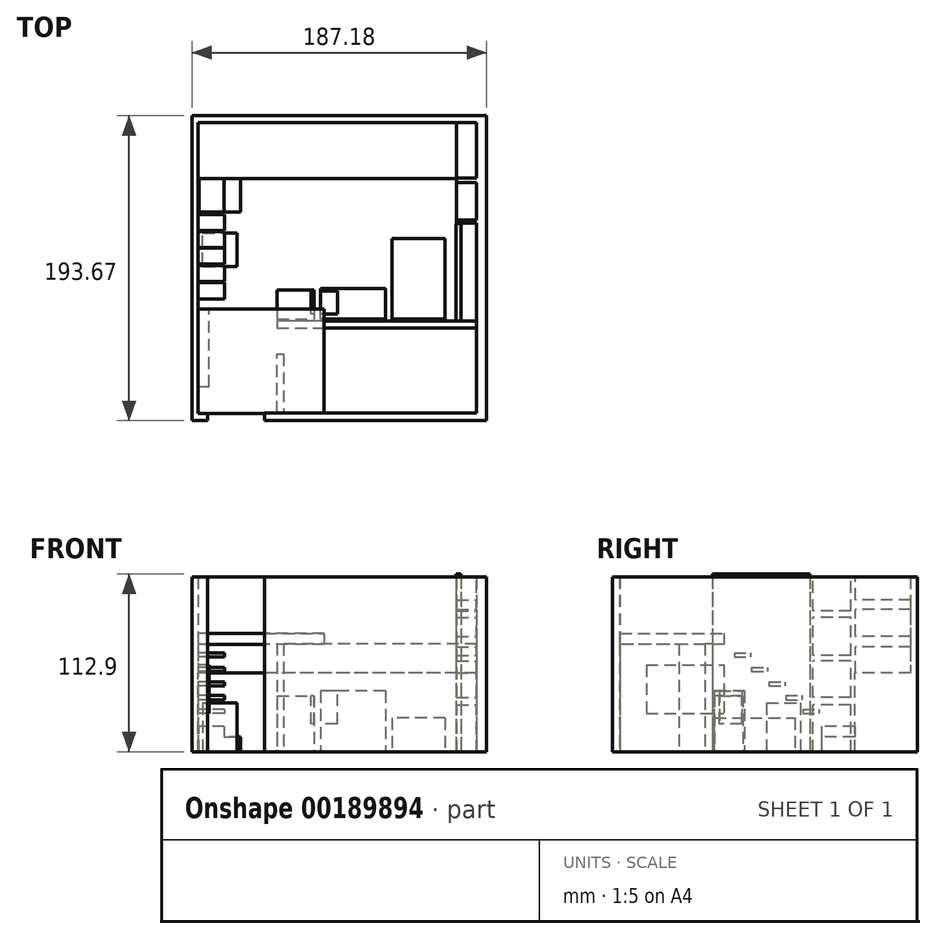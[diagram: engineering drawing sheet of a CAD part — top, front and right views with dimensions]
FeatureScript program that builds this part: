
annotation { "Feature Type Name" : "Feature", "Feature Type Description" : "" }
export const myFeature = defineFeature(function(context is Context, id is Id, definition is map)
    precondition{}
    {
        {
            var Q0;
            Q0=qCreatedBy(makeId("Top.planeOp"),FACE);
            var sketch = newSketch(context, id + "F0", { "sketchPlane" : qUnion([Q0])});
            skLineSegment(sketch, "E0", {"start": v(-29.04, -70.8) * mm, "end": v(-39.02, -70.8) * mm});
            skLineSegment(sketch, "E1", {"start": v(-39.02, -70.8) * mm, "end": v(-39.02, 122.87) * mm});
            skLineSegment(sketch, "E2", {"start": v(-39.02, 122.87) * mm, "end": v(148.16, 122.87) * mm});
            skLineSegment(sketch, "E3", {"start": v(148.16, 122.87) * mm, "end": v(148.16, -70.8) * mm});
            skLineSegment(sketch, "E4", {"start": v(148.16, -70.8) * mm, "end": v(7.05, -70.8) * mm});
            skLineSegment(sketch, "E5", {"start": v(7.05, -70.8) * mm, "end": v(7.05, -65.97) * mm});
            skLineSegment(sketch, "E6", {"start": v(7.05, -65.97) * mm, "end": v(141.88, -65.97) * mm});
            skLineSegment(sketch, "E7", {"start": v(141.88, -65.97) * mm, "end": v(141.88, 118.48) * mm});
            skLineSegment(sketch, "E8", {"start": v(141.88, 118.48) * mm, "end": v(-34.99, 118.48) * mm});
            skLineSegment(sketch, "E9", {"start": v(-34.99, 118.48) * mm, "end": v(-34.99, -66.3) * mm});
            skLineSegment(sketch, "E10", {"start": v(-34.99, -66.3) * mm, "end": v(-29.04, -66.3) * mm});
            skLineSegment(sketch, "E11", {"start": v(-29.04, -66.3) * mm, "end": v(-29.04, -70.8) * mm});
            skLineSegment(sketch, "E12", {"start": v(14.95, -65.97) * mm, "end": v(14.95, -28.61) * mm});
            skLineSegment(sketch, "E13", {"start": v(14.95, -28.61) * mm, "end": v(19.03, -28.61) * mm});
            skLineSegment(sketch, "E14", {"start": v(19.03, -28.61) * mm, "end": v(19.03, -65.97) * mm});
            skLineSegment(sketch, "E15", {"start": v(141.88, -7.47) * mm, "end": v(14.95, -7.47) * mm});
            skLineSegment(sketch, "E16", {"start": v(14.95, -7.47) * mm, "end": v(14.95, -12.15) * mm});
            skLineSegment(sketch, "E17", {"start": v(14.95, -12.15) * mm, "end": v(141.88, -12.15) * mm});
            skLineSegment(sketch, "E18", {"start": v(128.66, 54.4) * mm, "end": v(128.66, -7.47) * mm});
            skLineSegment(sketch, "E19", {"start": v(128.66, 54.4) * mm, "end": v(131.98, 54.4) * mm});
            skLineSegment(sketch, "E20", {"start": v(131.98, 54.4) * mm, "end": v(131.98, -7.47) * mm});
            skLineSegment(sketch, "E21.bottom", {"start": v(-34.45, 83.32) * mm, "end": v(-8.02, 83.32) * mm});
            skLineSegment(sketch, "E21.top", {"start": v(-34.45, 61.8) * mm, "end": v(-8.02, 61.8) * mm});
            skLineSegment(sketch, "E21.left", {"start": v(-34.45, 83.32) * mm, "end": v(-34.45, 61.8) * mm});
            skLineSegment(sketch, "E21.right", {"start": v(-8.02, 83.32) * mm, "end": v(-8.02, 61.8) * mm});
            skLineSegment(sketch, "E22.bottom", {"start": v(-8.02, 61.8) * mm, "end": v(-23.76, 61.8) * mm});
            skSolve(sketch);
        }
        {
            var Q0;
            Q0=makeQuery(id+"F0.imprint","IMPRINT",FACE,{"disambiguationData":[TD([[makeQuery(id+"F0.imprint","IMPRINT",EDGE,{"derivedFrom":sQuery(id+"F0.wireOp",EDGE,"E0")}),-1.0]])]});
            extrude(context, id + "F1", {"entities" : qUnion([Q0]), "depth" : 111 * mm});
        }
        {
            var Q0;
            Q0=makeQuery(id+"F1.opExtrude","SWEPT_FACE",FACE,{"disambiguationData":[OSD([sQuery(id+"F0.wireOp",EDGE,"E9")])]});
            var sketch = newSketch(context, id + "F2", { "sketchPlane" : qUnion([Q0])});
            skLineSegment(sketch, "E23", {"start": v(-66.3, 75.28) * mm, "end": v(0, 75.28) * mm});
            skLineSegment(sketch, "E24", {"start": v(0, 75.28) * mm, "end": v(0, 68.12) * mm});
            skLineSegment(sketch, "E25", {"start": v(0, 68.12) * mm, "end": v(-66.3, 68.12) * mm});
            skPoint(sketch, "E25.endSnap0", {"position": v(-66.3, 55.5) * mm});
            skLineSegment(sketch, "E26.bottom", {"start": v(-49.4, 55.11) * mm, "end": v(0, 55.11) * mm});
            skLineSegment(sketch, "E26.top", {"start": v(-49.4, 24.55) * mm, "end": v(0, 24.55) * mm});
            skLineSegment(sketch, "E26.left", {"start": v(-49.4, 55.11) * mm, "end": v(-49.4, 24.55) * mm});
            skLineSegment(sketch, "E26.right", {"start": v(0, 55.11) * mm, "end": v(0, 24.55) * mm});
            skLineSegment(sketch, "E27.bottom", {"start": v(118.48, 0) * mm, "end": v(83, 0) * mm});
            skLineSegment(sketch, "E27.top", {"start": v(118.48, 50.1) * mm, "end": v(83, 50.1) * mm});
            skLineSegment(sketch, "E27.left", {"start": v(118.48, 0) * mm, "end": v(118.48, 50.1) * mm});
            skLineSegment(sketch, "E27.right", {"start": v(83, 0) * mm, "end": v(83, 50.1) * mm});
            skLineSegment(sketch, "E28", {"start": v(0, 68.12) * mm, "end": v(83, 0) * mm, "construction": true});
            skLineSegment(sketch, "E29", {"start": v(-0.01, 75.35) * mm, "end": v(83, 7.23) * mm, "construction": true});
            skLineSegment(sketch, "E30.bottom", {"start": v(6.55, 62.74) * mm, "end": v(16.74, 62.74) * mm});
            skLineSegment(sketch, "E30.top", {"start": v(6.55, 60.17) * mm, "end": v(16.74, 60.17) * mm});
            skLineSegment(sketch, "E30.left", {"start": v(6.55, 62.74) * mm, "end": v(6.55, 60.17) * mm});
            skLineSegment(sketch, "E30.right", {"start": v(16.74, 62.74) * mm, "end": v(16.74, 60.17) * mm});
            skLineSegment(sketch, "E31.bottom", {"start": v(17.41, 53.62) * mm, "end": v(27.6, 53.62) * mm});
            skLineSegment(sketch, "E31.top", {"start": v(17.41, 51.05) * mm, "end": v(27.6, 51.05) * mm});
            skLineSegment(sketch, "E31.left", {"start": v(17.41, 53.62) * mm, "end": v(17.41, 51.05) * mm});
            skLineSegment(sketch, "E31.right", {"start": v(27.6, 53.62) * mm, "end": v(27.6, 51.05) * mm});
            skLineSegment(sketch, "E32.bottom", {"start": v(28.54, 44.5) * mm, "end": v(38.73, 44.5) * mm});
            skLineSegment(sketch, "E32.top", {"start": v(28.54, 41.93) * mm, "end": v(38.73, 41.93) * mm});
            skLineSegment(sketch, "E32.left", {"start": v(28.54, 44.5) * mm, "end": v(28.54, 41.93) * mm});
            skLineSegment(sketch, "E32.right", {"start": v(38.73, 44.5) * mm, "end": v(38.73, 41.93) * mm});
            skLineSegment(sketch, "E33.bottom", {"start": v(39.23, 35.68) * mm, "end": v(49.42, 35.68) * mm});
            skLineSegment(sketch, "E33.top", {"start": v(39.23, 33.1) * mm, "end": v(49.42, 33.1) * mm});
            skLineSegment(sketch, "E33.left", {"start": v(39.23, 35.68) * mm, "end": v(39.23, 33.1) * mm});
            skLineSegment(sketch, "E33.right", {"start": v(49.42, 35.68) * mm, "end": v(49.42, 33.1) * mm});
            skLineSegment(sketch, "E34.bottom", {"start": v(49.96, 27.02) * mm, "end": v(60.16, 27.02) * mm});
            skLineSegment(sketch, "E34.top", {"start": v(49.96, 24.45) * mm, "end": v(60.16, 24.45) * mm});
            skLineSegment(sketch, "E34.left", {"start": v(49.96, 27.02) * mm, "end": v(49.96, 24.45) * mm});
            skLineSegment(sketch, "E34.right", {"start": v(60.16, 27.02) * mm, "end": v(60.16, 24.45) * mm});
            skSolve(sketch);
        }
        {
            var Q0;
            {var subQ0=sQuery(id+"F2.wireOp",EDGE,"E23");Q0=makeQuery(id+"F2.imprint","IMPRINT",FACE,{"disambiguationData":[TD([[makeQuery(id+"F2.imprint","IMPRINT",EDGE,{"derivedFrom":subQ0}),-1.0]])]});}
            extrude(context, id + "F3", {"entities" : qUnion([Q0]), "operationType" : NewBodyOperationType.ADD, "depth" : 80 * mm});
        }
        {
            var Q0;
            Q0=qCreatedBy(makeId("Top.planeOp"),FACE);
            var sketch = newSketch(context, id + "F4", { "sketchPlane" : qUnion([Q0])});
            skLineSegment(sketch, "E35", {"start": v(88, -6.3) * mm, "end": v(88, 44.9) * mm});
            skLineSegment(sketch, "E36", {"start": v(88, 44.9) * mm, "end": v(121.84, 44.9) * mm});
            skLineSegment(sketch, "E37", {"start": v(121.84, 44.9) * mm, "end": v(121.84, -6.3) * mm});
            skLineSegment(sketch, "E38", {"start": v(121.84, -6.3) * mm, "end": v(88, -6.3) * mm});
            skLineSegment(sketch, "E39", {"start": v(83.82, 13.03) * mm, "end": v(83.82, -6.3) * mm});
            skLineSegment(sketch, "E40", {"start": v(83.82, -6.3) * mm, "end": v(42.79, -6.3) * mm});
            skLineSegment(sketch, "E41", {"start": v(42.79, -6.3) * mm, "end": v(42.79, 13.03) * mm});
            skLineSegment(sketch, "E42", {"start": v(83.82, 13.03) * mm, "end": v(42.79, 13.03) * mm});
            skLineSegment(sketch, "E43.bottom", {"start": v(-32.14, 26.93) * mm, "end": v(-10.27, 26.93) * mm});
            skLineSegment(sketch, "E43.top", {"start": v(-32.14, 48.42) * mm, "end": v(-10.27, 48.42) * mm});
            skLineSegment(sketch, "E43.left", {"start": v(-32.14, 26.93) * mm, "end": v(-32.14, 48.42) * mm});
            skLineSegment(sketch, "E43.right", {"start": v(-10.27, 26.93) * mm, "end": v(-10.27, 48.42) * mm});
            skLineSegment(sketch, "E44.bottom", {"start": v(15.18, 11.98) * mm, "end": v(38.65, 11.98) * mm});
            skLineSegment(sketch, "E44.top", {"start": v(15.18, -6.23) * mm, "end": v(38.65, -6.23) * mm});
            skLineSegment(sketch, "E44.left", {"start": v(15.18, 11.98) * mm, "end": v(15.18, -6.23) * mm});
            skLineSegment(sketch, "E44.right", {"start": v(38.65, 11.98) * mm, "end": v(38.65, -6.23) * mm});
            skSolve(sketch);
        }
        {
            var Q0;
            Q0=makeQuery(id+"F4.imprint","IMPRINT",FACE,{"disambiguationData":[TD([[makeQuery(id+"F4.imprint","IMPRINT",EDGE,{"derivedFrom":sQuery(id+"F4.wireOp",EDGE,"E35")}),-1.0]])]});
            extrude(context, id + "F5", {"entities" : qUnion([Q0]), "depth" : 21.5 * mm});
        }
        {
            var Q0;
            Q0=makeQuery(id+"F4.imprint","IMPRINT",FACE,{"disambiguationData":[TD([[makeQuery(id+"F4.imprint","IMPRINT",EDGE,{"derivedFrom":sQuery(id+"F4.wireOp",EDGE,"E39")}),-1.0]])]});
            extrude(context, id + "F6", {"entities" : qUnion([Q0]), "depth" : 38.7 * mm});
        }
        {
            var Q0;
            Q0=makeQuery(id+"F2.imprint","IMPRINT",FACE,{"disambiguationData":[TD([[makeQuery(id+"F2.imprint","IMPRINT",EDGE,{"derivedFrom":sQuery(id+"F2.wireOp",EDGE,"E26.bottom")}),-1.0]])]});
            extrude(context, id + "F7", {"entities" : qUnion([Q0]), "depth" : 6.9 * mm});
        }
        {
            var Q0;
            Q0=makeQuery(id+"F2.imprint","IMPRINT",FACE,{"disambiguationData":[TD([[makeQuery(id+"F2.imprint","IMPRINT",EDGE,{"derivedFrom":sQuery(id+"F2.wireOp",EDGE,"E27.bottom")}),-1.0]])]});
            extrude(context, id + "F8", {"entities" : qUnion([Q0]), "operationType" : NewBodyOperationType.ADD, "depth" : 177 * mm});
        }
        {
            var Q0;
            Q0=makeQuery(id+"F1.opExtrude","SWEPT_FACE",FACE,{"disambiguationData":[OSD([sQuery(id+"F0.wireOp",EDGE,"E7")])]});
            var sketch = newSketch(context, id + "F9", { "sketchPlane" : qUnion([Q0])});
            skLineSegment(sketch, "E45.bottom", {"start": v(-50.34, 0) * mm, "end": v(-38.16, 0) * mm});
            skLineSegment(sketch, "E46.bottom", {"start": v(-38.16, 0) * mm, "end": v(-25, 0) * mm});
            skLineSegment(sketch, "E47.bottom", {"start": v(-17.9, 0) * mm, "end": v(-7.53, 0) * mm});
            skLineSegment(sketch, "E48.bottom", {"start": v(-8.39, 0) * mm, "end": v(-7.53, 0) * mm});
            skLineSegment(sketch, "E49", {"start": v(-83.28, 50.1) * mm, "end": v(-83.28, 111) * mm});
            skLineSegment(sketch, "E50", {"start": v(-118.48, 66.78) * mm, "end": v(-83.28, 66.78) * mm});
            skLineSegment(sketch, "E51", {"start": v(-118.48, 90.3) * mm, "end": v(-83.28, 90.3) * mm});
            skLineSegment(sketch, "E52", {"start": v(-80.5, 0) * mm, "end": v(-80.5, 111) * mm});
            skLineSegment(sketch, "E53", {"start": v(-56.47, 0) * mm, "end": v(-56.47, 111) * mm});
            skLineSegment(sketch, "E54", {"start": v(-80.5, 29.81) * mm, "end": v(-56.47, 29.81) * mm});
            skLineSegment(sketch, "E55", {"start": v(-80.5, 34.44) * mm, "end": v(-56.47, 34.44) * mm});
            skLineSegment(sketch, "E56", {"start": v(-80.5, 57.78) * mm, "end": v(-56.47, 57.78) * mm});
            skLineSegment(sketch, "E57", {"start": v(-80.5, 61.29) * mm, "end": v(-56.47, 61.29) * mm});
            skLineSegment(sketch, "E58", {"start": v(-80.5, 85.31) * mm, "end": v(-56.47, 85.31) * mm});
            skLineSegment(sketch, "E59", {"start": v(-80.5, 89.4) * mm, "end": v(-56.47, 89.4) * mm});
            skLineSegment(sketch, "E60", {"start": v(-118.48, 73.36) * mm, "end": v(-83.28, 73.36) * mm});
            skLineSegment(sketch, "E61", {"start": v(-118.48, 96.47) * mm, "end": v(-83.28, 96.47) * mm});
            skLineSegment(sketch, "E62.0", {"start": v(-118.48, 111) * mm, "end": v(-118.48, 50.1) * mm});
            skLineSegment(sketch, "E63.0", {"start": v(65.97, 0) * mm, "end": v(-118.48, 0) * mm});
            skLineSegment(sketch, "E64.0", {"start": v(65.97, 111) * mm, "end": v(-118.48, 111) * mm});
            skLineSegment(sketch, "E65", {"start": v(-54.66, 111) * mm, "end": v(-54.66, 0) * mm});
            skSolve(sketch);
        }
        {
            var Q0;
            {var subQ0=sQuery(id+"F9.wireOp",EDGE,"E50");Q0=makeQuery(id+"F9.imprint","IMPRINT",FACE,{"disambiguationData":[TD([[makeQuery(id+"F9.imprint","IMPRINT",EDGE,{"derivedFrom":subQ0}),1.0]])]});}
            var Q1;
            {var subQ0=sQuery(id+"F9.wireOp",EDGE,"E51");Q1=makeQuery(id+"F9.imprint","IMPRINT",FACE,{"disambiguationData":[TD([[makeQuery(id+"F9.imprint","IMPRINT",EDGE,{"derivedFrom":subQ0}),1.0]])]});}
            var Q2;
            {var subQ0=sQuery(id+"F9.wireOp",EDGE,"E54");Q2=makeQuery(id+"F9.imprint","IMPRINT",FACE,{"disambiguationData":[TD([[makeQuery(id+"F9.imprint","IMPRINT",EDGE,{"derivedFrom":subQ0}),1.0]])]});}
            var Q3;
            {var subQ0=sQuery(id+"F9.wireOp",EDGE,"E56");Q3=makeQuery(id+"F9.imprint","IMPRINT",FACE,{"disambiguationData":[TD([[makeQuery(id+"F9.imprint","IMPRINT",EDGE,{"derivedFrom":subQ0}),1.0]])]});}
            var Q4;
            {var subQ0=sQuery(id+"F9.wireOp",EDGE,"E58");Q4=makeQuery(id+"F9.imprint","IMPRINT",FACE,{"disambiguationData":[TD([[makeQuery(id+"F9.imprint","IMPRINT",EDGE,{"derivedFrom":subQ0}),1.0]])]});}
            var Q5;
            {var subQ8=makeQuery(id+"F1.opExtrude","SWEPT_FACE",FACE,{"disambiguationData":[OSD([sQuery(id+"F0.wireOp",EDGE,"E7")])]});var subQ14=makeQuery(id+"F8.boolean.opBoolean","INTERSECT",EDGE,{"derivedFrom":[subQ8,makeQuery(id+"F8.opExtrude","SWEPT_FACE",FACE,{"disambiguationData":[OSD([sQuery(id+"F2.wireOp",EDGE,"E27.right")])]})]});Q5=makeQuery(id+"F9.imprint","IMPRINT",FACE,{"disambiguationData":[TD([[makeQuery(id+"F9.imprint","IMPRINT",EDGE,{"derivedFrom":subQ14}),-1.0]])]});}
            var Q6;
            {var subQ7=sQuery(id+"F9.wireOp",EDGE,"E65");Q6=makeQuery(id+"F9.imprint","IMPRINT",FACE,{"disambiguationData":[TD([[makeQuery(id+"F9.imprint","IMPRINT",EDGE,{"derivedFrom":subQ7}),-1.0]])]});}
            extrude(context, id + "F10", {"entities" : qUnion([Q0, Q1, Q2, Q3, Q4, Q5, Q6]), "operationType" : NewBodyOperationType.ADD, "depth" : 12.8 * mm});
        }
        {
            var Q0;
            {var subQ0=sQuery(id+"F0.wireOp",EDGE,"E18");Q0=makeQuery(id+"F0.imprint","IMPRINT",FACE,{"disambiguationData":[TD([[makeQuery(id+"F0.imprint","IMPRINT",EDGE,{"derivedFrom":subQ0}),1.0]])]});}
            extrude(context, id + "F11", {"entities" : qUnion([Q0]), "operationType" : NewBodyOperationType.ADD, "depth" : 112.9 * mm});
        }
        {
            var Q0;
            {var subQ0=sQuery(id+"F0.wireOp",EDGE,"E16");Q0=makeQuery(id+"F0.imprint","IMPRINT",FACE,{"disambiguationData":[TD([[makeQuery(id+"F0.imprint","IMPRINT",EDGE,{"derivedFrom":subQ0}),1.0]])]});}
            var Q1;
            {var subQ0=sQuery(id+"F0.wireOp",EDGE,"E12");Q1=makeQuery(id+"F0.imprint","IMPRINT",FACE,{"disambiguationData":[TD([[makeQuery(id+"F0.imprint","IMPRINT",EDGE,{"derivedFrom":subQ0}),-1.0]])]});}
            extrude(context, id + "F12", {"entities" : qUnion([Q0, Q1]), "depth" : 68.6 * mm});
        }
        {
            var Q0;
            Q0=makeQuery(id+"F2.imprint","IMPRINT",FACE,{"disambiguationData":[TD([[makeQuery(id+"F2.imprint","IMPRINT",EDGE,{"derivedFrom":sQuery(id+"F2.wireOp",EDGE,"E30.bottom")}),-1.0]])]});
            var Q1;
            Q1=makeQuery(id+"F2.imprint","IMPRINT",FACE,{"disambiguationData":[TD([[makeQuery(id+"F2.imprint","IMPRINT",EDGE,{"derivedFrom":sQuery(id+"F2.wireOp",EDGE,"E31.bottom")}),-1.0]])]});
            var Q2;
            Q2=makeQuery(id+"F2.imprint","IMPRINT",FACE,{"disambiguationData":[TD([[makeQuery(id+"F2.imprint","IMPRINT",EDGE,{"derivedFrom":sQuery(id+"F2.wireOp",EDGE,"E32.bottom")}),-1.0]])]});
            var Q3;
            Q3=makeQuery(id+"F2.imprint","IMPRINT",FACE,{"disambiguationData":[TD([[makeQuery(id+"F2.imprint","IMPRINT",EDGE,{"derivedFrom":sQuery(id+"F2.wireOp",EDGE,"E33.bottom")}),-1.0]])]});
            var Q4;
            Q4=makeQuery(id+"F2.imprint","IMPRINT",FACE,{"disambiguationData":[TD([[makeQuery(id+"F2.imprint","IMPRINT",EDGE,{"derivedFrom":sQuery(id+"F2.wireOp",EDGE,"E34.bottom")}),-1.0]])]});
            extrude(context, id + "F13", {"entities" : qUnion([Q0, Q1, Q2, Q3, Q4]), "operationType" : NewBodyOperationType.ADD, "depth" : 16.7 * mm});
        }
        {
            var Q0;
            Q0=makeQuery(id+"F4.imprint","IMPRINT",FACE,{"disambiguationData":[TD([[makeQuery(id+"F4.imprint","IMPRINT",EDGE,{"derivedFrom":sQuery(id+"F4.wireOp",EDGE,"E43.bottom")}),1.0]])]});
            var Q1;
            Q1=sQuery(id+"F4.wireOp",EDGE,"E43.top");
            var Q2;
            Q2=sQuery(id+"F4.wireOp",EDGE,"E43.left");
            var Q3;
            Q3=sQuery(id+"F4.wireOp",EDGE,"E43.bottom");
            var Q4;
            Q4=sQuery(id+"F4.wireOp",EDGE,"E43.right");
            extrude(context, id + "F14", {"entities" : qUnion([Q0]), "surfaceEntities" : qUnion([Q1, Q2, Q3, Q4]), "depth" : 31 * mm});
        }
        {
            var Q0;
            Q0=makeQuery(id+"F0.imprint","IMPRINT",FACE,{"disambiguationData":[TD([[makeQuery(id+"F0.imprint","IMPRINT",EDGE,{"derivedFrom":sQuery(id+"F0.wireOp",EDGE,"E21.bottom")}),-1.0]])]});
            extrude(context, id + "F15", {"entities" : qUnion([Q0]), "operationType" : NewBodyOperationType.ADD, "depth" : 9.5 * mm});
        }
        {
            var Q0;
            Q0=makeQuery(id+"F15.opExtrude","CAP_FACE",FACE,{"disambiguationData":[OSD([sQuery(id+"F0.wireOp",EDGE,"E21.bottom"),sQuery(id+"F0.wireOp",EDGE,"E21.top"),sQuery(id+"F0.wireOp",EDGE,"E21.left"),sQuery(id+"F0.wireOp",EDGE,"E21.right"),sQuery(id+"F0.wireOp",EDGE,"E22.bottom")])],"isStart":false});
            var sketch = newSketch(context, id + "F16", { "sketchPlane" : qUnion([Q0])});
            skLineSegment(sketch, "E66", {"start": v(-18.48, 61.8) * mm, "end": v(-18.48, 83) * mm});
            skLineSegment(sketch, "E67.0", {"start": v(-8.02, 83) * mm, "end": v(-34.45, 83) * mm});
            skLineSegment(sketch, "E67.1", {"start": v(-34.45, 83) * mm, "end": v(-34.45, 61.8) * mm});
            skLineSegment(sketch, "E67.2", {"start": v(-34.45, 61.8) * mm, "end": v(-8.02, 61.8) * mm});
            skSolve(sketch);
        }
        {
            var Q0;
            {var subQ0=sQuery(id+"F16.wireOp",EDGE,"E66");Q0=makeQuery(id+"F16.imprint","IMPRINT",FACE,{"disambiguationData":[TD([[makeQuery(id+"F16.imprint","IMPRINT",EDGE,{"derivedFrom":subQ0}),1.0]])]});}
            extrude(context, id + "F17", {"entities" : qUnion([Q0]), "operationType" : NewBodyOperationType.ADD, "depth" : 6.7 * mm});
        }
        {
            var Q0;
            Q0=makeQuery(id+"F4.imprint","IMPRINT",FACE,{"disambiguationData":[TD([[makeQuery(id+"F4.imprint","IMPRINT",EDGE,{"derivedFrom":sQuery(id+"F4.wireOp",EDGE,"E44.bottom")}),-1.0]])]});
            extrude(context, id + "F18", {"entities" : qUnion([Q0]), "depth" : 35.6 * mm});
        }
        {
            var Q0;
            Q0=makeQuery(id+"F6.opExtrude","CAP_FACE",FACE,{"disambiguationData":[OSD([sQuery(id+"F4.wireOp",EDGE,"E39"),sQuery(id+"F4.wireOp",EDGE,"E40"),sQuery(id+"F4.wireOp",EDGE,"E41"),sQuery(id+"F4.wireOp",EDGE,"E42")])],"isStart":false});
            var sketch = newSketch(context, id + "F19", { "sketchPlane" : qUnion([Q0])});
            skLineSegment(sketch, "E68.bottom", {"start": v(53.47, -3) * mm, "end": v(36.69, -3) * mm});
            skLineSegment(sketch, "E68.top", {"start": v(53.47, 11.41) * mm, "end": v(36.69, 11.41) * mm});
            skLineSegment(sketch, "E68.left", {"start": v(53.47, -3) * mm, "end": v(53.47, 11.41) * mm});
            skLineSegment(sketch, "E68.right", {"start": v(36.69, -3) * mm, "end": v(36.69, 11.41) * mm});
            skSolve(sketch);
        }
        {
            var Q0;
            Q0 = qSketchRegion(id + "F19", true);
            extrude(context, id + "F20", {"entities" : qUnion([Q0]), "operationType" : NewBodyOperationType.REMOVE, "oppositeDirection" : true, "depth" : 21.1 * mm});
        }
    });
